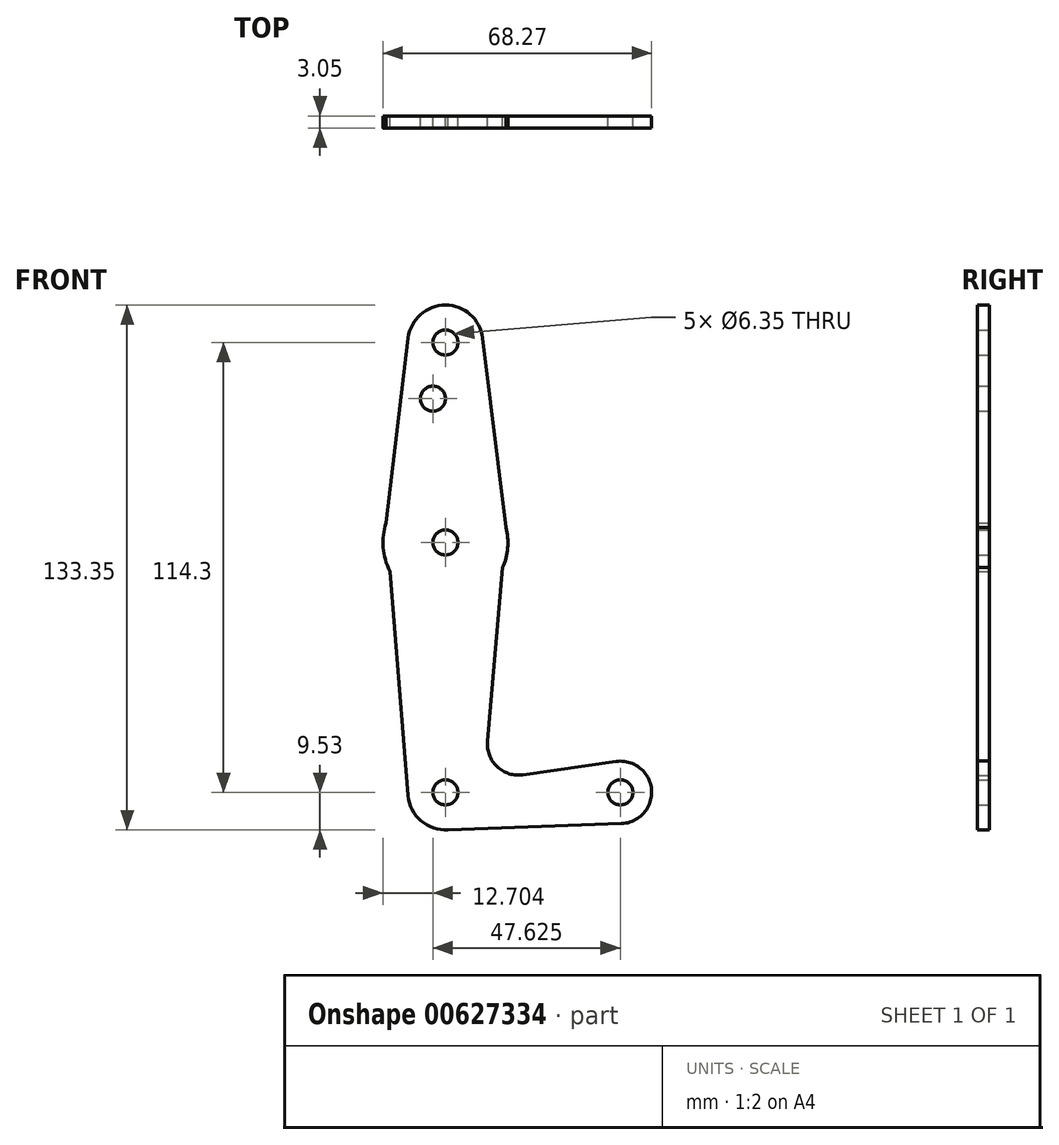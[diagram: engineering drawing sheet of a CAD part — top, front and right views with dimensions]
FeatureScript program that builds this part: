
annotation { "Feature Type Name" : "Feature", "Feature Type Description" : "" }
export const myFeature = defineFeature(function(context is Context, id is Id, definition is map)
    precondition{}
    {
        {
            var Q0;
            Q0=qCreatedBy(makeId("Front.planeOp"),FACE);
            var sketch = newSketch(context, id + "F0", { "sketchPlane" : qUnion([Q0])});
            skLineSegment(sketch, "E0", {"start": v(-22.5, 57.15) * mm, "end": v(-22.5, -57.15) * mm, "construction": true});
            skLineSegment(sketch, "E1", {"start": v(-22.5, -57.15) * mm, "end": v(21.95, -57.15) * mm, "construction": true});
            skPoint(sketch, "E2.centerSnap0", {"position": v(-22.5, 0) * mm});
            skCircle(sketch, "E3", {"center": v(-22.5, -57.15) * mm, "radius": 9.53 * mm});
            skCircle(sketch, "E4", {"center": v(21.95, -57.15) * mm, "radius": 7.94 * mm});
            skCircle(sketch, "E5", {"center": v(-22.5, 57.15) * mm, "radius": 9.53 * mm});
            skCircle(sketch, "E6", {"center": v(-22.5, 6.35) * mm, "radius": 15.88 * mm});
            skLineSegment(sketch, "E7", {"start": v(-31.96, 58.28) * mm, "end": v(-37.57, 11.33) * mm});
            skLineSegment(sketch, "E8", {"start": v(-7.09, 10.15) * mm, "end": v(-13.05, 58.32) * mm});
            skLineSegment(sketch, "E9", {"start": v(-37.57, 11.33) * mm, "end": v(-32, -57.91) * mm});
            skLineSegment(sketch, "E10", {"start": v(-7.09, 10.15) * mm, "end": v(-11.8, -44.14) * mm});
            skLineSegment(sketch, "E11", {"start": v(-2.75, -52.7) * mm, "end": v(20.81, -49.3) * mm});
            skLineSegment(sketch, "E12", {"start": v(-22.5, -66.68) * mm, "end": v(22.23, -65.08) * mm});
            skCircle(sketch, "E13", {"center": v(-25.68, 42.88) * mm, "radius": 3.18 * mm});
            skCircle(sketch, "E14", {"center": v(-22.5, -57.15) * mm, "radius": 3.18 * mm});
            skCircle(sketch, "E15", {"center": v(21.95, -57.15) * mm, "radius": 3.18 * mm});
            skCircle(sketch, "E16", {"center": v(-22.5, 6.35) * mm, "radius": 3.18 * mm});
            skCircle(sketch, "E17", {"center": v(-22.5, 57.15) * mm, "radius": 3.18 * mm});
            skPoint(sketch, "E18.newPointB", {"position": v(-22.5, -55.55) * mm});
            skArc(sketch, "E18.filletArc", {"start": v(-11.8, -44.14) * mm, "mid": v(-9.35, -50.6) * mm, "end": v(-2.75, -52.7) * mm});
            skSolve(sketch);
        }
        {
            var Q0;
            Q0 = qSketchRegion(id + "F0", true);
            extrude(context, id + "F1", {"entities" : qUnion([Q0]), "depth" : 3.05 * mm, "offsetDistance" : 25.4 * mm});
        }
    });
